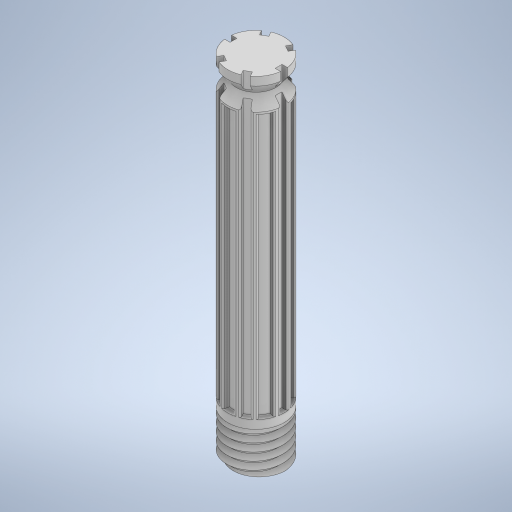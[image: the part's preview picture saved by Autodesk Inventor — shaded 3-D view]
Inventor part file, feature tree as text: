
AUTODESK INVENTOR PART (.ipt)
format: ipt  version: 2024 (Build 280153000, 153)  size: 549,376 bytes
history: native  units: mm
features: sketch x7, extrude x5, pattern_circular x2, fillet x2, other x1, revolve x1
ambient origin geometry x8: Origin, YZ Plane, XZ Plane, XY Plane, X Axis, Y Axis, Z Axis, Center Point
bodies: Volumenkörper1 (feature_tree)
feature tree (18):
  extrude  "Extrusion1"  Depth=10.0mm TaperAngle=0.0deg
  other  "Spirale1"
  extrude  "Extrusion9"  Depth=3.5mm
  revolve  "Umdrehung1"
  extrude  "Extrusion6"  Depth=2.0mm
  pattern_circular  "Runde Anordnung1"  Count=4  [1 undecoded]
  extrude  "Extrusion7"  Depth=0.2mm TaperAngle=360.0deg
  pattern_circular  "Runde Anordnung2"  [2 undecoded]
  fillet  "Rundung4"  Radius=25.0mm
  fillet  "Rundung5"  Radius=60.0mm
  extrude  "Extrusion8"  Depth=0.29mm
  sketch  "Skizze1"  dims[d0=10.0mm d1=61.7mm d2=0.0mm]
  sketch  "Skizze6"  dims[d20=1.5mm d21=3.5mm]
  sketch  "Skizze8"  dims[d22=2.0mm d23=2.0mm]
  sketch  "Skizze9"  dims[d24=90.0deg]
  sketch  "Skizze12"  dims[d32=1.0mm]
  sketch  "Skizze13"  dims[d33=0.6mm]
  sketch  "Skizze14"  dims[d34=0.6mm d35=40.0mm d36=21.85mm d37=0.0mm d38=0.0mm d39=60.0mm d40=360.0deg d42=1.0mm d43=25.0mm d44=21.85mm d45=0.0mm d46=0.0mm d47=60.0mm d48=360.0deg d50=0.29mm d51=1.0mm d52=0.29mm d53=8.0mm d54=10.0mm d56=1.4mm d58=1.4mm d59=9.85mm d60=10.0mm d61=0.0mm d62=90.0deg d63=90.0deg d64=0.0mm d65=0.0mm d66=1.5mm d67=0.0mm d68=10.0mm d69=52.8mm d70=0.0mm d71=60.0deg d72=0.2mm d55=0.0mm]
note: 3 required parameter values undecoded (feature->parameter linkage not recoverable at this tier; creation-order binding heuristic only, values carry confidence <= 0.55)
